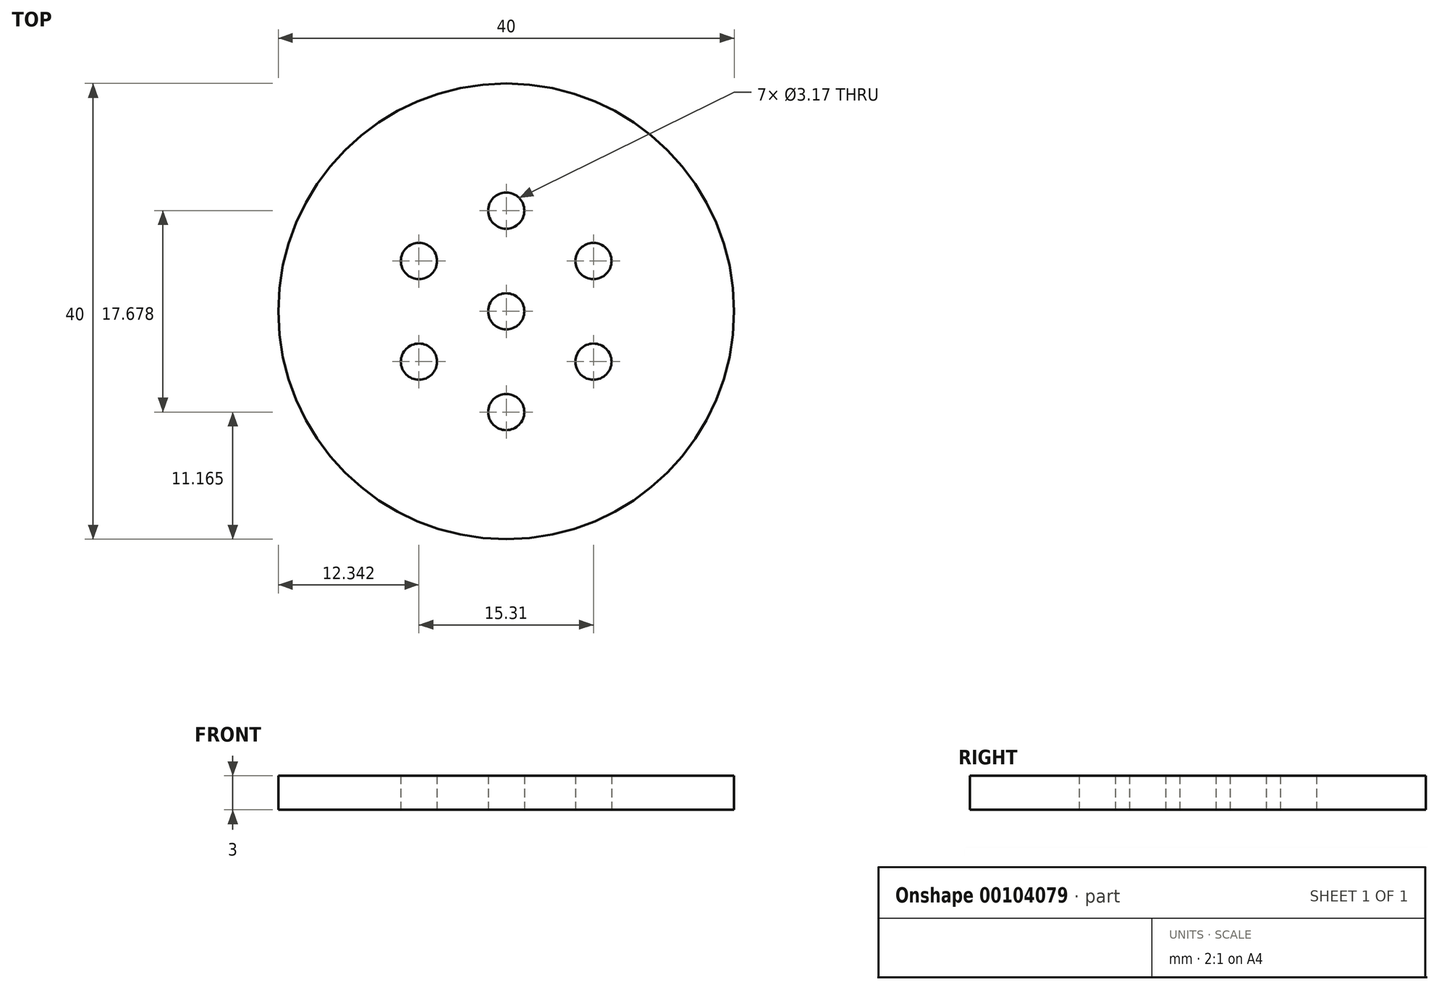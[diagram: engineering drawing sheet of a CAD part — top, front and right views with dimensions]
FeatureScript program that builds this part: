
annotation { "Feature Type Name" : "Feature", "Feature Type Description" : "" }
export const myFeature = defineFeature(function(context is Context, id is Id, definition is map)
    precondition{}
    {
        {
            var Q0;
            Q0=qCreatedBy(makeId("Top.planeOp"),FACE);
            var sketch = newSketch(context, id + "F0", { "sketchPlane" : qUnion([Q0])});
            skCircle(sketch, "E0", {"center": v(-36.16, 9.98) * mm, "radius": 1.59 * mm});
            skCircle(sketch, "E1", {"center": v(-36.16, 9.98) * mm, "radius": 20 * mm});
            skCircle(sketch, "E2", {"center": v(-36.16, 18.82) * mm, "radius": 1.59 * mm});
            skCircle(sketch, "E3.1.0", {"center": v(-43.82, 14.4) * mm, "radius": 1.59 * mm});
            skCircle(sketch, "E3.2.0", {"center": v(-43.82, 5.56) * mm, "radius": 1.59 * mm});
            skCircle(sketch, "E3.3.0", {"center": v(-36.16, 1.14) * mm, "radius": 1.59 * mm});
            skCircle(sketch, "E3.4.0", {"center": v(-28.5, 5.56) * mm, "radius": 1.59 * mm});
            skCircle(sketch, "E3.5.0", {"center": v(-28.5, 14.4) * mm, "radius": 1.59 * mm});
            skSolve(sketch);
        }
        {
            var Q0;
            Q0=makeQuery(id+"F0.imprint","IMPRINT",FACE,{"disambiguationData":[TD([[makeQuery(id+"F0.imprint","IMPRINT",EDGE,{"derivedFrom":sQuery(id+"F0.wireOp",EDGE,"E0")}),-1.0]])]});
            extrude(context, id + "F1", {"entities" : qUnion([Q0]), "depth" : 3 * mm});
        }
    });
